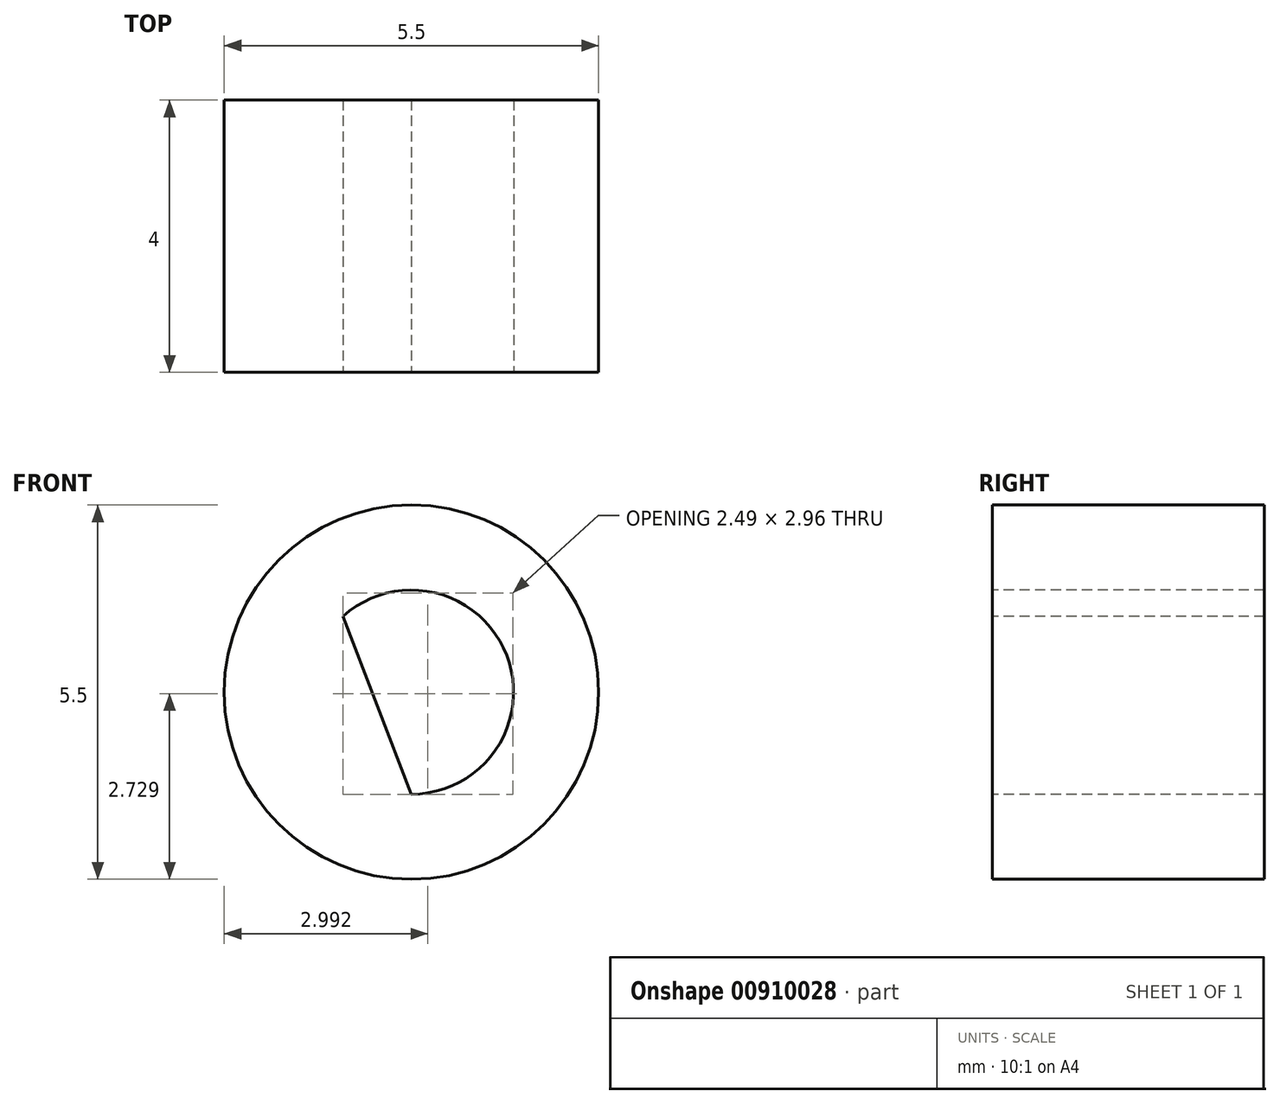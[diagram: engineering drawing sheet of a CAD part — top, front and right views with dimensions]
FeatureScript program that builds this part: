
annotation { "Feature Type Name" : "Feature", "Feature Type Description" : "" }
export const myFeature = defineFeature(function(context is Context, id is Id, definition is map)
    precondition{}
    {
        {
            var Q0;
            Q0=qCreatedBy(makeId("Front.planeOp"),FACE);
            var sketch = newSketch(context, id + "F0", { "sketchPlane" : qUnion([Q0])});
            skCircle(sketch, "E0", {"center": v(0, 0) * mm, "radius": 2.75 * mm});
            skSolve(sketch);
        }
        {
            var Q0;
            Q0=makeQuery(id+"F0.imprint","IMPRINT",FACE,{"disambiguationData":[TD([[makeQuery(id+"F0.imprint","IMPRINT",EDGE,{"derivedFrom":sQuery(id+"F0.wireOp",EDGE,"E0")}),1.0]])]});
            extrude(context, id + "F1", {"entities" : qUnion([Q0]), "depth" : 4 * mm, "offsetDistance" : 25.4 * mm});
        }
        {
            var Q0;
            Q0=makeQuery(id+"F1.opExtrude","CAP_FACE",FACE,{"disambiguationData":[OSD([sQuery(id+"F0.wireOp",EDGE,"E0")])],"isStart":false});
            var sketch = newSketch(context, id + "F2", { "sketchPlane" : qUnion([Q0])});
            skArc(sketch, "E1", {"start": v(0, -1.5) * mm, "mid": v(1.4, 0.54) * mm, "end": v(-1, 1.11) * mm});
            skLineSegment(sketch, "E2", {"start": v(-1, 1.11) * mm, "end": v(0, -1.5) * mm});
            skSolve(sketch);
        }
        {
            var Q0;
            Q0=makeQuery(id+"F2.imprint","IMPRINT",FACE,{"disambiguationData":[TD([[makeQuery(id+"F2.imprint","IMPRINT",EDGE,{"derivedFrom":sQuery(id+"F2.wireOp",EDGE,"E1")}),1.0]])]});
            extrude(context, id + "F3", {"entities" : qUnion([Q0]), "operationType" : NewBodyOperationType.REMOVE, "endBound" : BoundingType.THROUGH_ALL, "oppositeDirection" : true, "depth" : 101.6 * mm, "offsetDistance" : 25.4 * mm});
        }
    });
